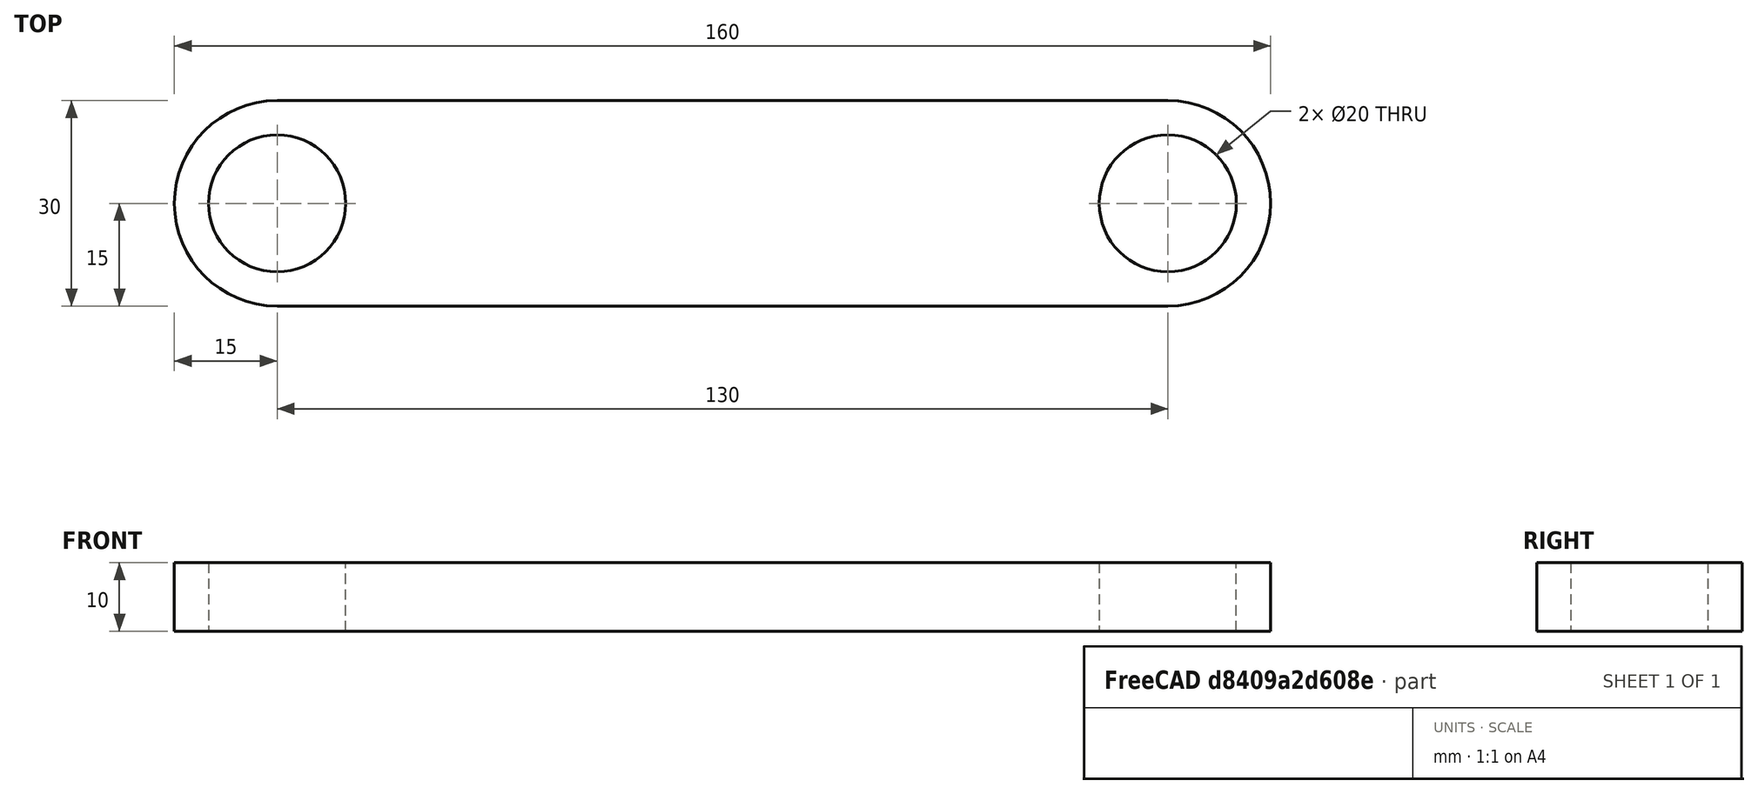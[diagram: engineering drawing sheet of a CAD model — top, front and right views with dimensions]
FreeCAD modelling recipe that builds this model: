
FCSTD DOCUMENT  (FreeCAD 0.17RUnknown)
Label: aaa
License: All rights reserved
LicenseURL: http://en.wikipedia.org/wiki/All_rights_reserved
objects: Sketcher::SketchObject×1, PartDesign::Pad×1, PartDesign::Body×1
note: 4 computed .brp shape members not serialized (recipe doc carries the construction recipe); baked Part::Feature solids carry a one-line shape summary decoded from their .brp

FEATURE [Sketcher::SketchObject] Sketch
  MapMode = 5
  Support = -> [XY_Plane]
  sketch-geometry (6):
    g0: LineSegment StartX=-1e-12 StartY=15 StartZ=0 EndX=130 EndY=15 EndZ=0
    g1: LineSegment StartX=130 StartY=-15 StartZ=0 EndX=6e-12 EndY=-15 EndZ=0
    g2: ArcOfCircle CenterX=0 CenterY=0 CenterZ=0 NormalX=0 NormalY=0 NormalZ=1 AngleXU=0 Radius=15 StartAngle=1.5708 EndAngle=4.71239
    g3: ArcOfCircle CenterX=130 CenterY=0 CenterZ=0 NormalX=0 NormalY=0 NormalZ=1 AngleXU=0 Radius=15 StartAngle=4.71239 EndAngle=7.85398
    g4: Circle CenterX=0 CenterY=0 CenterZ=0 NormalX=0 NormalY=0 NormalZ=1 AngleXU=0 Radius=10
    g5: Circle CenterX=130 CenterY=0 CenterZ=0 NormalX=0 NormalY=0 NormalZ=1 AngleXU=0 Radius=10
  constraints (17):
    c: Horizontal(g0)
    c: Horizontal(g1)
    c: Equal(g0,g1)
    c: Coincident(g2,g0)
    c: Coincident(g2,g1)
    c: Coincident(g3,g0)
    c: Coincident(g3,g1)
    c: Distance(g0,g1) = 30
    c: Angle(g2) = 3.14159
    c: Angle(g3) = 3.14159
    c: Distance(g0) = 130
    c: Coincident(g2,g-1)
    c: PointOnObject(g0,g-2)
    c: Coincident(g4,g-1)
    c: Radius(g4) = 10
    c: Coincident(g5,g3)
    c: Radius(g5) = 10
FEATURE [PartDesign::Pad] Pad
  Length = 10
  Length2 = 100
  Profile = -> Sketch
  Type = 0
FEATURE [PartDesign::Body] Body
  Group = -> [Sketch,Pad]
  Origin = -> Origin
  Tip = -> Pad
